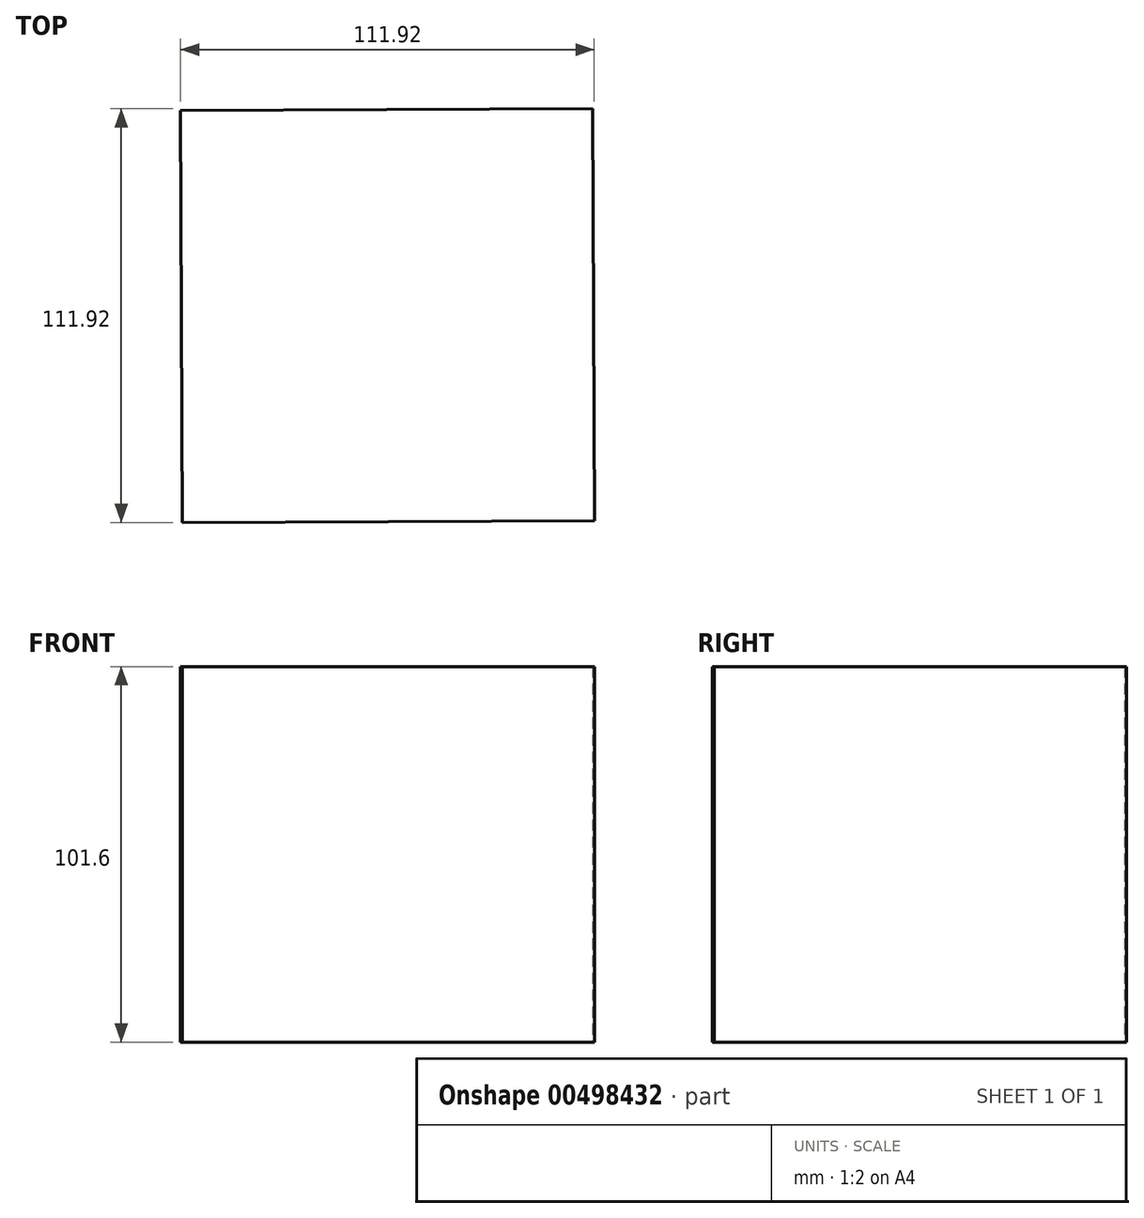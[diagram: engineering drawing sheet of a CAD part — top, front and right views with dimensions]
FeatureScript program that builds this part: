
annotation { "Feature Type Name" : "Feature", "Feature Type Description" : "" }
export const myFeature = defineFeature(function(context is Context, id is Id, definition is map)
    precondition{}
    {
        {
            var Q0;
            Q0=qCreatedBy(makeId("Top.planeOp"),FACE);
            var sketch = newSketch(context, id + "F0", { "sketchPlane" : qUnion([Q0])});
            skCircle(sketch, "E0.cCircle", {"center": v(0, 0) * mm, "radius": 78.84 * mm, "construction": true});
            skLineSegment(sketch, "E0.0", {"start": v(55.53, 55.96) * mm, "end": v(55.96, -55.53) * mm});
            skLineSegment(sketch, "E0.1", {"start": v(55.96, -55.53) * mm, "end": v(-55.53, -55.96) * mm});
            skLineSegment(sketch, "E0.2", {"start": v(-55.53, -55.96) * mm, "end": v(-55.96, 55.53) * mm});
            skLineSegment(sketch, "E0.3", {"start": v(-55.96, 55.53) * mm, "end": v(55.53, 55.96) * mm});
            skSolve(sketch);
        }
        {
            var Q0;
            Q0=makeQuery(id+"F0.imprint","IMPRINT",FACE,{"disambiguationData":[TD([[makeQuery(id+"F0.imprint","IMPRINT",EDGE,{"derivedFrom":sQuery(id+"F0.wireOp",EDGE,"E0.0")}),-1.0]])]});
            extrude(context, id + "F1", {"entities" : qUnion([Q0]), "depth" : 101.6 * mm, "offsetDistance" : 25.4 * mm, "symmetric" : true});
        }
    });
